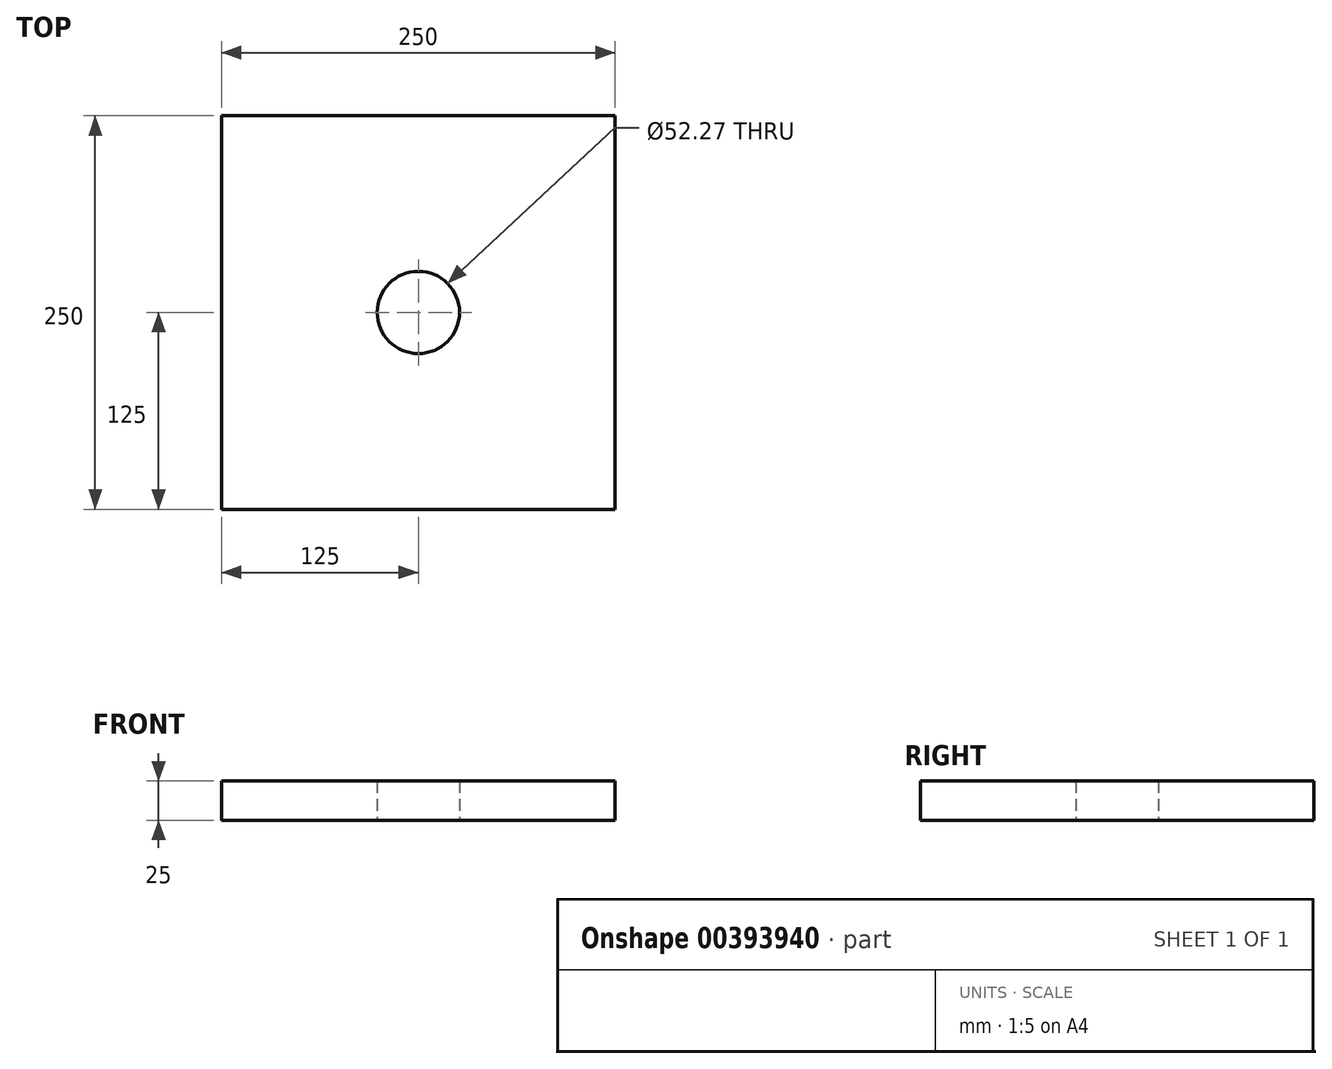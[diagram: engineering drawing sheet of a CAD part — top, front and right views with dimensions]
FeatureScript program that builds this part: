
annotation { "Feature Type Name" : "Feature", "Feature Type Description" : "" }
export const myFeature = defineFeature(function(context is Context, id is Id, definition is map)
    precondition{}
    {
        {
            var Q0;
            Q0=qCreatedBy(makeId("Top.planeOp"),FACE);
            var sketch = newSketch(context, id + "F0", { "sketchPlane" : qUnion([Q0])});
            skLineSegment(sketch, "E0.bottom", {"start": v(125, 125) * mm, "end": v(-125, 125) * mm});
            skLineSegment(sketch, "E0.top", {"start": v(125, -125) * mm, "end": v(-125, -125) * mm});
            skLineSegment(sketch, "E0.left", {"start": v(125, 125) * mm, "end": v(125, -125) * mm});
            skLineSegment(sketch, "E0.right", {"start": v(-125, 125) * mm, "end": v(-125, -125) * mm});
            skPoint(sketch, "E0.middle", {"position": v(0, 0) * mm});
            skCircle(sketch, "E1", {"center": v(0, 0) * mm, "radius": 26.13 * mm});
            skSolve(sketch);
        }
        {
            var Q0;
            Q0=makeQuery(id+"F0.imprint","IMPRINT",FACE,{"disambiguationData":[TD([[makeQuery(id+"F0.imprint","IMPRINT",EDGE,{"derivedFrom":sQuery(id+"F0.wireOp",EDGE,"E0.bottom")}),1.0]])]});
            extrude(context, id + "F1", {"entities" : qUnion([Q0]), "depth" : 25 * mm, "offsetDistance" : 25 * mm});
        }
    });
